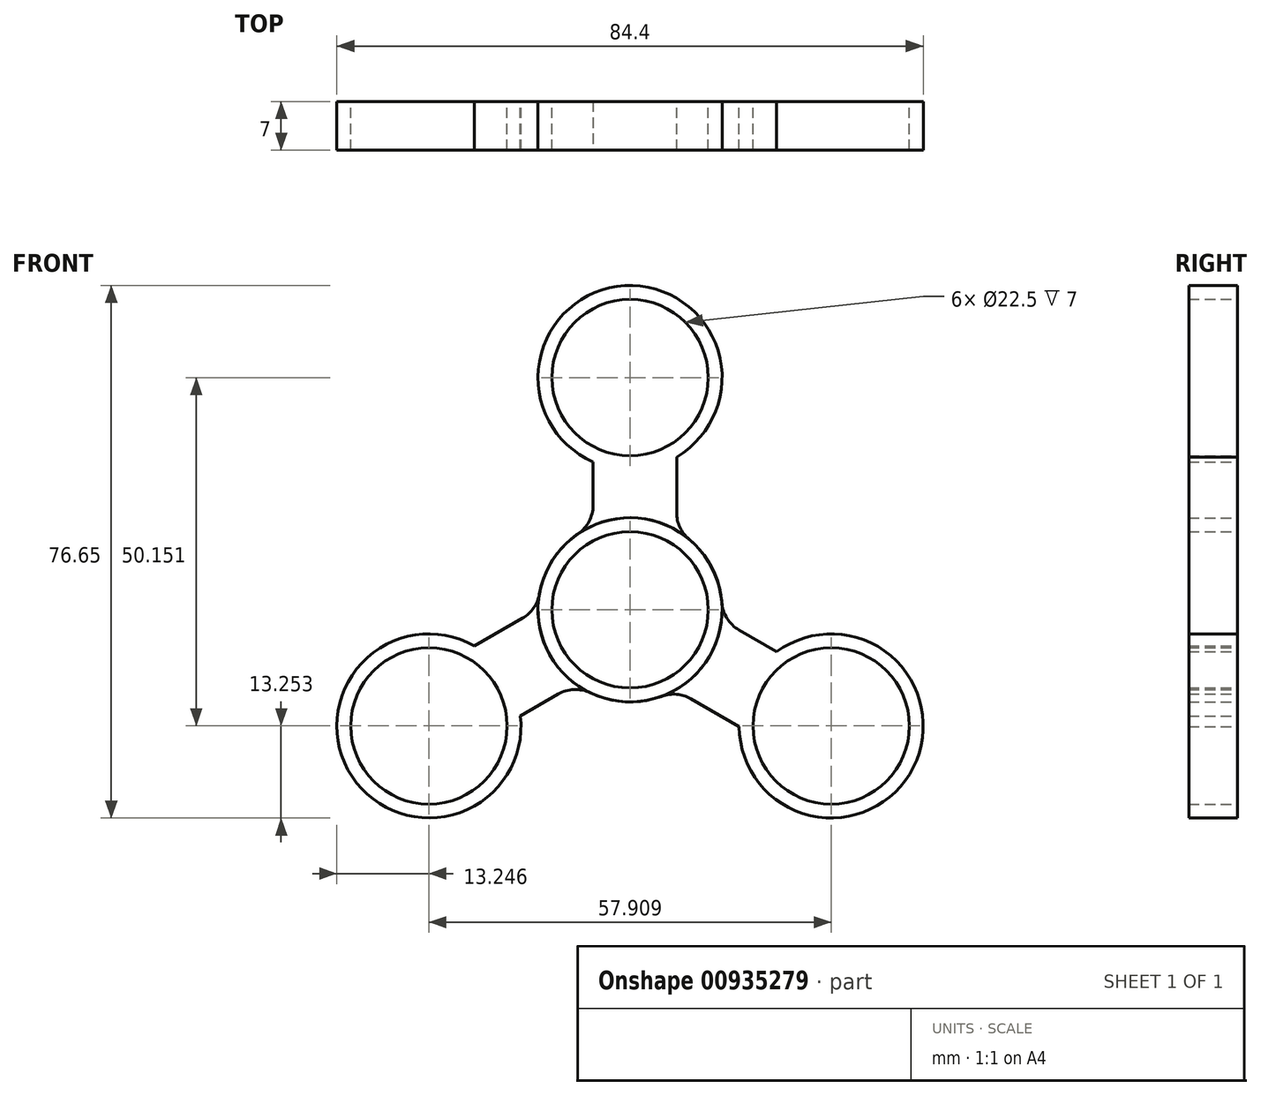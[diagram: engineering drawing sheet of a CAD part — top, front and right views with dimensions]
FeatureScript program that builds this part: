
annotation { "Feature Type Name" : "Feature", "Feature Type Description" : "" }
export const myFeature = defineFeature(function(context is Context, id is Id, definition is map)
    precondition{}
    {
        {
            var Q0;
            Q0=qCreatedBy(makeId("Front.planeOp"),FACE);
            var sketch = newSketch(context, id + "F0", { "sketchPlane" : qUnion([Q0])});
            skCircle(sketch, "E0", {"center": v(0, 0) * mm, "radius": 11.25 * mm});
            skCircle(sketch, "E1.0", {"center": v(0, 0) * mm, "radius": 13.25 * mm});
            skCircle(sketch, "E2", {"center": v(0, 33.43) * mm, "radius": 11.25 * mm});
            skCircle(sketch, "E3.0", {"center": v(0, 33.43) * mm, "radius": 13.25 * mm});
            skLineSegment(sketch, "E4", {"start": v(-5.33, 21.3) * mm, "end": v(-5.33, 12.13) * mm});
            skLineSegment(sketch, "E5", {"start": v(6.7, 22) * mm, "end": v(6.7, 11.43) * mm});
            skSolve(sketch);
        }
        {
            var Q0;
            {var subQ0=sQuery(id+"F0.wireOp",EDGE,"E4");Q0=makeQuery(id+"F0.imprint","IMPRINT",FACE,{"disambiguationData":[TD([[makeQuery(id+"F0.imprint","IMPRINT",EDGE,{"derivedFrom":subQ0}),1.0]])]});}
            var Q1;
            Q1=makeQuery(id+"F0.imprint","IMPRINT",FACE,{"disambiguationData":[TD([[makeQuery(id+"F0.imprint","IMPRINT",EDGE,{"derivedFrom":sQuery(id+"F0.wireOp",EDGE,"E2")}),-1.0]])]});
            var Q2;
            Q2=makeQuery(id+"F0.imprint","IMPRINT",FACE,{"disambiguationData":[TD([[makeQuery(id+"F0.imprint","IMPRINT",EDGE,{"derivedFrom":sQuery(id+"F0.wireOp",EDGE,"E0")}),-1.0]])]});
            extrude(context, id + "F1", {"entities" : qUnion([Q0, Q1, Q2]), "depth" : 7 * mm, "offsetDistance" : 25 * mm});
        }
        {
            var Q0;
            Q0=makeQuery(id+"F1.opExtrude","SWEPT_BODY",BODY,{"disambiguationData":[OSD([sQuery(id+"F0.wireOp",EDGE,"E0"),sQuery(id+"F0.wireOp",EDGE,"E1.0"),sQuery(id+"F0.wireOp",EDGE,"E2"),sQuery(id+"F0.wireOp",EDGE,"E3.0"),sQuery(id+"F0.wireOp",EDGE,"E4"),sQuery(id+"F0.wireOp",EDGE,"E5")])]});
            var Q1;
            Q1=makeQuery(id+"F1.opExtrude","CAP_EDGE",EDGE,{"disambiguationData":[OSD([sQuery(id+"F0.wireOp",EDGE,"E0")])],"isStart":false});
            circularPattern(context, id + "F2", {"entities" : qUnion([Q0]), "axis" : qUnion([Q1]), "angle" : 360 * degree, "instanceCount" : 3, "equalSpace" : true});
        }
        {
            var Q0;
            Q0=makeQuery(id+"F1.opExtrude","SWEPT_EDGE",EDGE,{"disambiguationData":[OSD([sQuery(id+"F0.wireOp",EDGE,"E1.0"),sQuery(id+"F0.wireOp",EDGE,"E5")])]});
            var Q1;
            Q1=makeQuery(id+"F2.opPattern","COPY",EDGE,{"derivedFrom":makeQuery(id+"F1.opExtrude","SWEPT_EDGE",EDGE,{"disambiguationData":[OSD([sQuery(id+"F0.wireOp",EDGE,"E1.0"),sQuery(id+"F0.wireOp",EDGE,"E4")])]}),"instanceName":"2"});
            var Q2;
            Q2=makeQuery(id+"F2.opPattern","COPY",EDGE,{"derivedFrom":makeQuery(id+"F1.opExtrude","SWEPT_EDGE",EDGE,{"disambiguationData":[OSD([sQuery(id+"F0.wireOp",EDGE,"E1.0"),sQuery(id+"F0.wireOp",EDGE,"E5")])]}),"instanceName":"2"});
            var Q3;
            Q3=makeQuery(id+"F2.opPattern","COPY",EDGE,{"derivedFrom":makeQuery(id+"F1.opExtrude","SWEPT_EDGE",EDGE,{"disambiguationData":[OSD([sQuery(id+"F0.wireOp",EDGE,"E1.0"),sQuery(id+"F0.wireOp",EDGE,"E4")])]}),"instanceName":"1"});
            var Q4;
            Q4=makeQuery(id+"F2.opPattern","COPY",EDGE,{"derivedFrom":makeQuery(id+"F1.opExtrude","SWEPT_EDGE",EDGE,{"disambiguationData":[OSD([sQuery(id+"F0.wireOp",EDGE,"E1.0"),sQuery(id+"F0.wireOp",EDGE,"E5")])]}),"instanceName":"1"});
            var Q5;
            Q5=makeQuery(id+"F1.opExtrude","SWEPT_EDGE",EDGE,{"disambiguationData":[OSD([sQuery(id+"F0.wireOp",EDGE,"E1.0"),sQuery(id+"F0.wireOp",EDGE,"E4")])]});
            fillet(context, id + "F3", {"entities" : qUnion([Q0, Q1, Q2, Q3, Q4, Q5]), "radius" : 5 * mm, "tangentPropagation" : true, "allowEdgeOverflow" : false});
        }
    });
